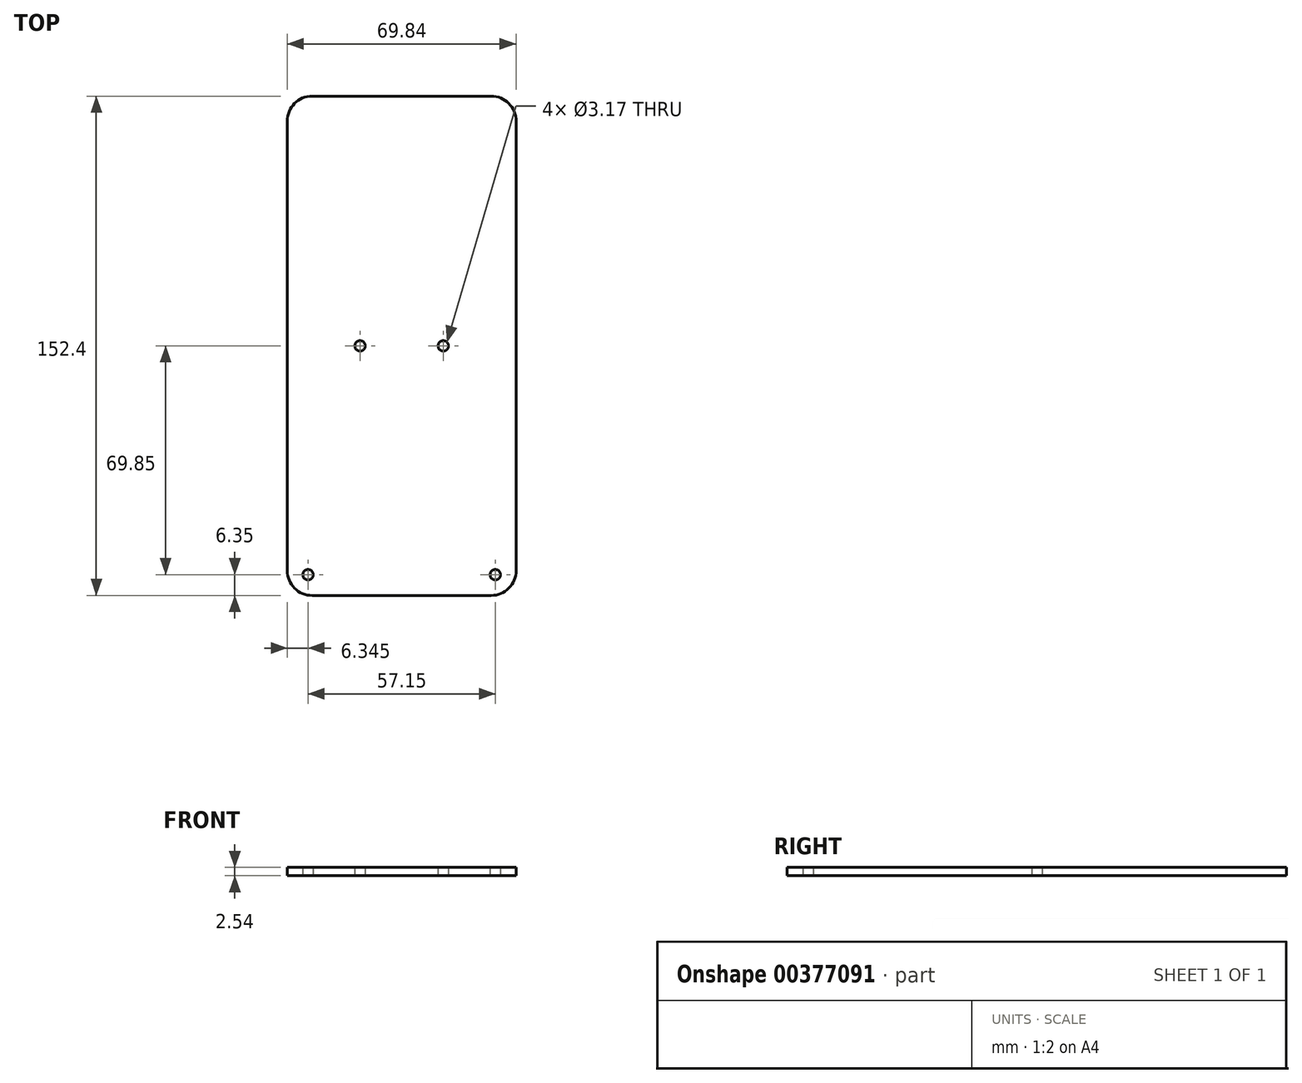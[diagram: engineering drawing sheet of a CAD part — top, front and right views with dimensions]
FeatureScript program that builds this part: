
annotation { "Feature Type Name" : "Feature", "Feature Type Description" : "" }
export const myFeature = defineFeature(function(context is Context, id is Id, definition is map)
    precondition{}
    {
        {
            var Q0;
            Q0=qCreatedBy(makeId("Top.planeOp"),FACE);
            var sketch = newSketch(context, id + "F0", { "sketchPlane" : qUnion([Q0])});
            skLineSegment(sketch, "E0.bottom", {"start": v(34.92, 76.2) * mm, "end": v(-34.93, 76.2) * mm});
            skLineSegment(sketch, "E0.top", {"start": v(34.93, -76.2) * mm, "end": v(-34.92, -76.2) * mm});
            skLineSegment(sketch, "E0.left", {"start": v(34.92, 76.2) * mm, "end": v(34.93, -76.2) * mm});
            skLineSegment(sketch, "E0.right", {"start": v(-34.93, 76.2) * mm, "end": v(-34.92, -76.2) * mm});
            skPoint(sketch, "E0.middle", {"position": v(0, 0) * mm});
            skCircle(sketch, "E1", {"center": v(-12.7, 0) * mm, "radius": 1.59 * mm});
            skCircle(sketch, "E2", {"center": v(12.7, 0) * mm, "radius": 1.59 * mm});
            skLineSegment(sketch, "E3", {"start": v(-12.7, 0) * mm, "end": v(12.7, 0) * mm, "construction": true});
            skPoint(sketch, "E4.middle", {"position": v(0, -69.85) * mm});
            skCircle(sketch, "E5", {"center": v(-28.57, -69.85) * mm, "radius": 1.59 * mm});
            skCircle(sketch, "E6", {"center": v(28.57, -69.85) * mm, "radius": 1.59 * mm});
            skLineSegment(sketch, "E7", {"start": v(-28.57, -69.85) * mm, "end": v(28.57, -69.85) * mm, "construction": true});
            skLineSegment(sketch, "E8", {"start": v(0, 0) * mm, "end": v(0, -69.85) * mm, "construction": true});
            skSolve(sketch);
        }
        {
            var Q0;
            Q0=makeQuery(id+"F0.imprint","IMPRINT",FACE,{"disambiguationData":[TD([[makeQuery(id+"F0.imprint","IMPRINT",EDGE,{"derivedFrom":sQuery(id+"F0.wireOp",EDGE,"E0.bottom")}),1.0]])]});
            extrude(context, id + "F1", {"entities" : qUnion([Q0]), "depth" : 2.54 * mm});
        }
        {
            var Q0;
            Q0=makeQuery(id+"F1.opExtrude","SWEPT_EDGE",EDGE,{"disambiguationData":[OSD([sQuery(id+"F0.wireOp",EDGE,"E0.bottom"),sQuery(id+"F0.wireOp",EDGE,"E0.right")])]});
            var Q1;
            Q1=makeQuery(id+"F1.opExtrude","SWEPT_EDGE",EDGE,{"disambiguationData":[OSD([sQuery(id+"F0.wireOp",EDGE,"E0.bottom"),sQuery(id+"F0.wireOp",EDGE,"E0.left")])]});
            var Q2;
            Q2=makeQuery(id+"F1.opExtrude","SWEPT_EDGE",EDGE,{"disambiguationData":[OSD([sQuery(id+"F0.wireOp",EDGE,"E0.top"),sQuery(id+"F0.wireOp",EDGE,"E0.right")])]});
            var Q3;
            Q3=makeQuery(id+"F1.opExtrude","SWEPT_EDGE",EDGE,{"disambiguationData":[OSD([sQuery(id+"F0.wireOp",EDGE,"E0.top"),sQuery(id+"F0.wireOp",EDGE,"E0.left")])]});
            fillet(context, id + "F2", {"entities" : qUnion([Q0, Q1, Q2, Q3]), "radius" : 7.62 * mm, "tangentPropagation" : true, "allowEdgeOverflow" : false});
        }
    });
